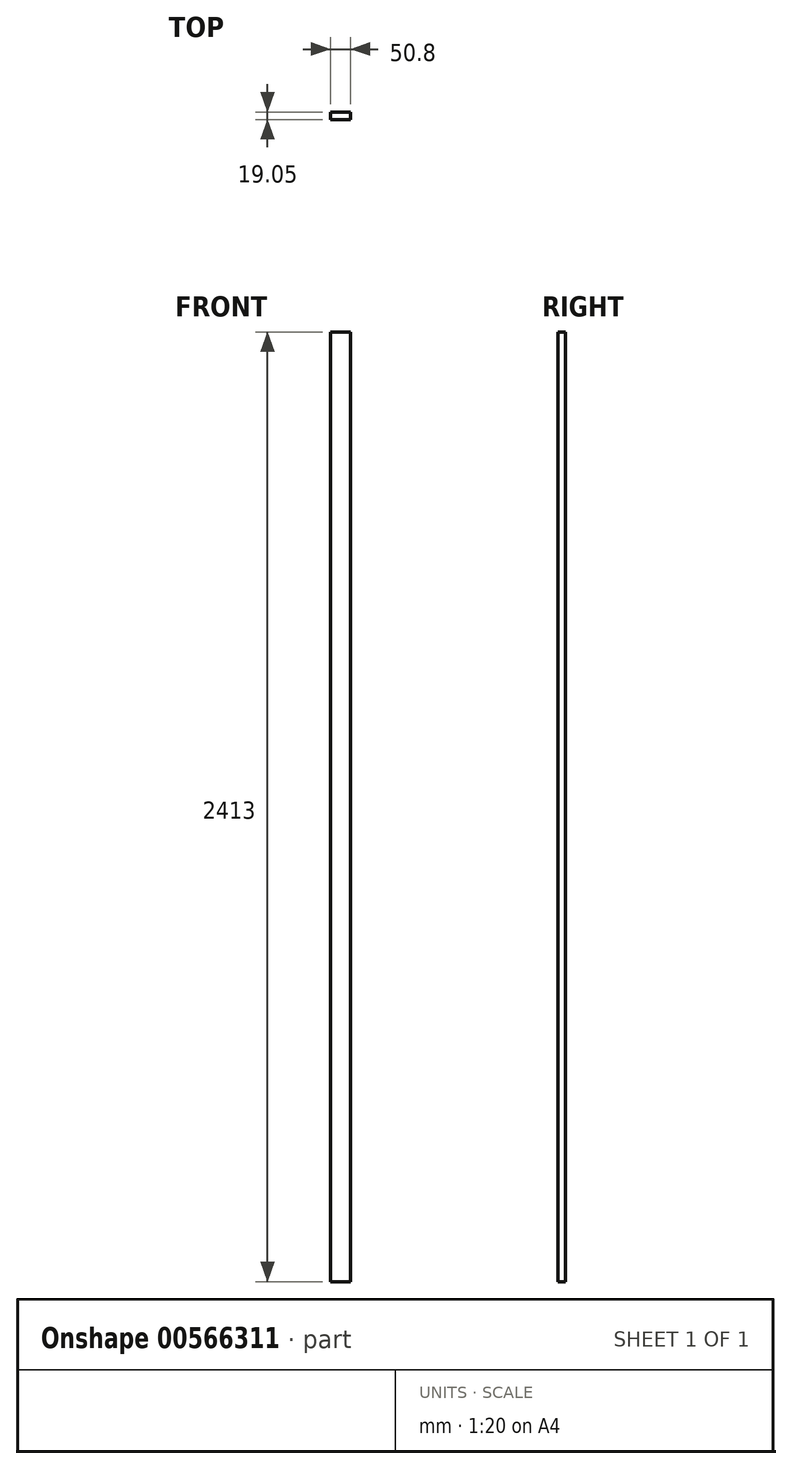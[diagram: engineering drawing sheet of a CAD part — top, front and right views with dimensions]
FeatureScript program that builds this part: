
annotation { "Feature Type Name" : "Feature", "Feature Type Description" : "" }
export const myFeature = defineFeature(function(context is Context, id is Id, definition is map)
    precondition{}
    {
        {
            var Q0;
            Q0=qCreatedBy(makeId("Front.planeOp"),FACE);
            var sketch = newSketch(context, id + "F0", { "sketchPlane" : qUnion([Q0])});
            skLineSegment(sketch, "E0.bottom", {"start": v(0, 0) * mm, "end": v(50.8, 0) * mm});
            skLineSegment(sketch, "E0.top", {"start": v(0, 2413) * mm, "end": v(50.8, 2413) * mm});
            skLineSegment(sketch, "E0.left", {"start": v(0, 0) * mm, "end": v(0, 2413) * mm});
            skLineSegment(sketch, "E0.right", {"start": v(50.8, 0) * mm, "end": v(50.8, 2413) * mm});
            skSolve(sketch);
        }
        {
            var Q0;
            Q0=makeQuery(id+"F0.imprint","IMPRINT",FACE,{"disambiguationData":[TD([[makeQuery(id+"F0.imprint","IMPRINT",EDGE,{"derivedFrom":sQuery(id+"F0.wireOp",EDGE,"E0.bottom")}),1.0]])]});
            extrude(context, id + "F1", {"entities" : qUnion([Q0]), "depth" : 19.05 * mm, "offsetDistance" : 25.4 * mm});
        }
    });
